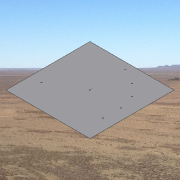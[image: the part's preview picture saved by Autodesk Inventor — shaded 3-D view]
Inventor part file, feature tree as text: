
AUTODESK INVENTOR PART (.ipt)
format: ipt  version: 2014 SP1 (Build 180222100, 222)  size: 148,480 bytes
history: native  units: in
note: dims shown in document units (in); Inventor stores cm internally (conversion verified against a paired STEP export)
features: extrude x3, sketch x3
ambient origin geometry x8: Origin, YZ Plane, XZ Plane, XY Plane, X Axis, Y Axis, Z Axis, Center Point
bodies: Solid1 (feature_tree)
feature tree (6):
  extrude  "Extrusion1"  Depth=787.4016in
  extrude  "Extrusion2"  Depth=1.0in
  extrude  "Extrusion3"  Depth=1.0in
  sketch  "Sketch1"  dims[d0=787.4016in d1=787.4016in]
  sketch  "Sketch2"  dims[d2=1.0in d3=0.0in d4=10.0in]
  sketch  "Sketch3"  dims[d5=10.0in d6=331.8898in d7=10.0in d8=289.3701in d9=1.1811in d11=360.0deg d13=1.1811in d15=60.0deg d17=1.0in d18=0.0in d19=1.0in d20=1.0in d21=19.0in d22=1.0in d23=0.0in]
